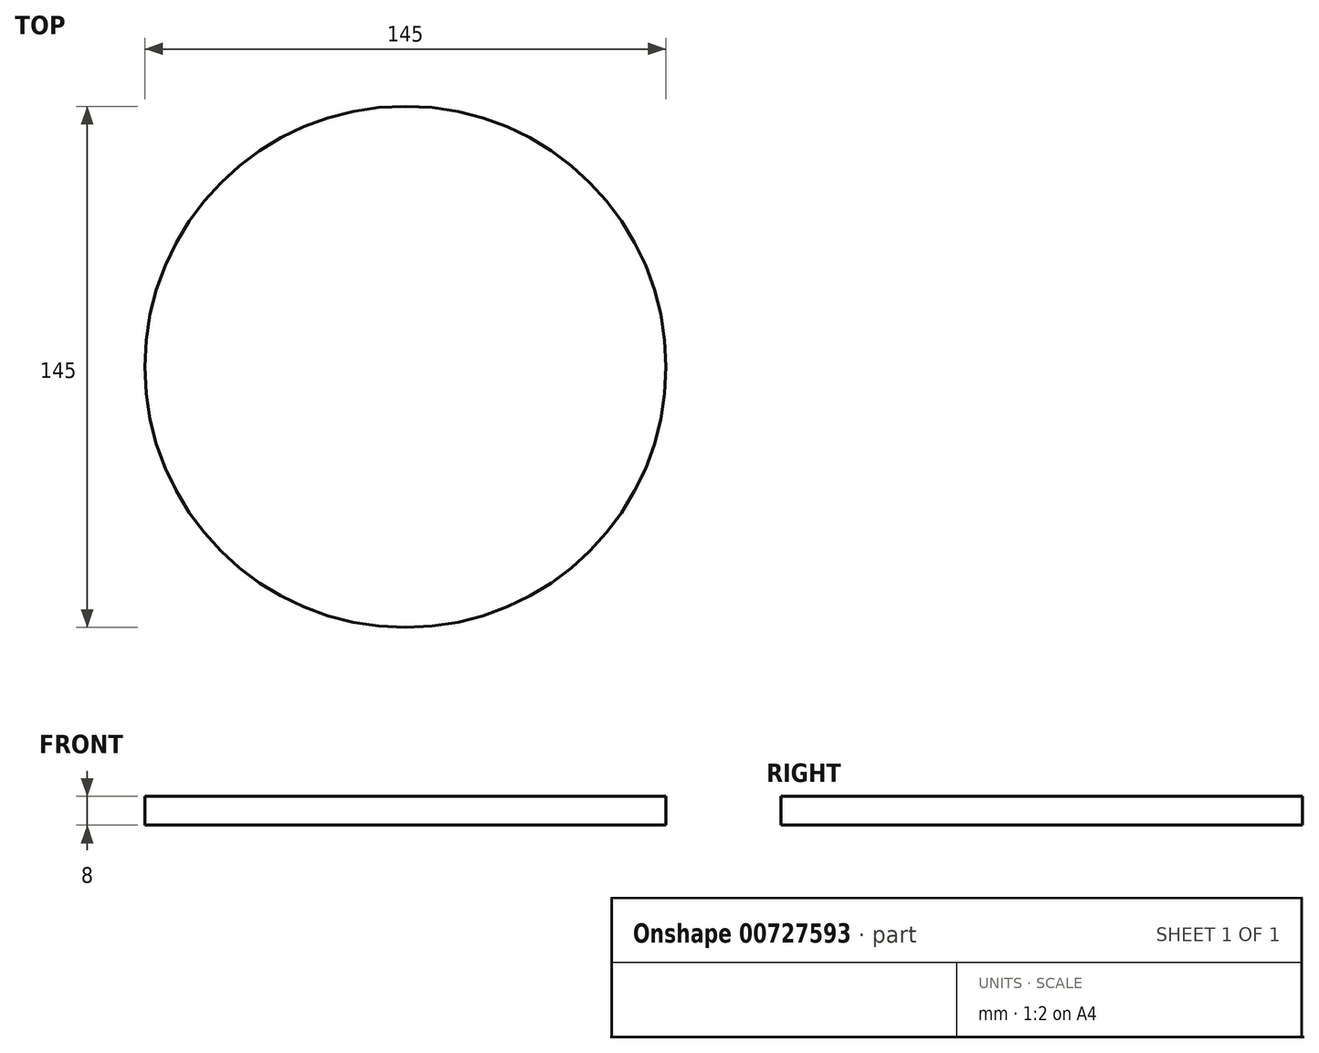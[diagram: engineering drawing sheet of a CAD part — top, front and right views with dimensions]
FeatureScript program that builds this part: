
annotation { "Feature Type Name" : "Feature", "Feature Type Description" : "" }
export const myFeature = defineFeature(function(context is Context, id is Id, definition is map)
    precondition{}
    {
        {
            var Q0;
            Q0=qCreatedBy(makeId("Top.planeOp"),FACE);
            var sketch = newSketch(context, id + "F0", { "sketchPlane" : qUnion([Q0])});
            skCircle(sketch, "E0", {"center": v(0, 0) * mm, "radius": 72.5 * mm});
            skSolve(sketch);
        }
        {
            var Q0;
            Q0=makeQuery(id+"F0.imprint","IMPRINT",FACE,{"disambiguationData":[TD([[makeQuery(id+"F0.imprint","IMPRINT",EDGE,{"derivedFrom":sQuery(id+"F0.wireOp",EDGE,"E0")}),1.0]])]});
            var Q1;
            Q1=sQuery(id+"F0.wireOp",EDGE,"E0");
            extrude(context, id + "F1", {"entities" : qUnion([Q0]), "surfaceEntities" : qUnion([Q1]), "depth" : 8 * mm, "offsetDistance" : 25.4 * mm});
        }
        {
            var Q0;
            Q0=qCreatedBy(makeId("Top.planeOp"),FACE);
            var sketch = newSketch(context, id + "F2", { "sketchPlane" : qUnion([Q0])});
            skLineSegment(sketch, "E1", {"start": v(-53.15, 29.78) * mm, "end": v(-22.76, 29.78) * mm});
            skLineSegment(sketch, "E2", {"start": v(-53.15, 29.78) * mm, "end": v(-53.15, 27.36) * mm});
            skLineSegment(sketch, "E3", {"start": v(-53.15, 27.36) * mm, "end": v(-39.89, 2.28) * mm});
            skLineSegment(sketch, "E4", {"start": v(-39.89, 2.28) * mm, "end": v(-33.01, 2.28) * mm});
            skLineSegment(sketch, "E5", {"start": v(-33.01, 2.28) * mm, "end": v(-45.31, 25.55) * mm});
            skLineSegment(sketch, "E6", {"start": v(-45.31, 25.55) * mm, "end": v(-33.01, 25.55) * mm});
            skLineSegment(sketch, "E7", {"start": v(-22.76, 29.78) * mm, "end": v(-21.8, 13.86) * mm});
            skLineSegment(sketch, "E8", {"start": v(-21.8, 13.86) * mm, "end": v(-22.76, 13.86) * mm});
            skFitSpline(sketch, "E9", {"points": [v(-33.01, 25.55) * mm, v(-29.28, 25.55) * mm], "startDerivative": vector(3.74, 0) * mm, "endDerivative": vector(3.74, 0) * mm});
            skFitSpline(sketch, "E10", {"points": [v(-29.28, 25.55) * mm, v(-27.1, 24.47) * mm, v(-24.7, 22.06) * mm, v(-23.6, 18.56) * mm, v(-22.76, 13.86) * mm], "startDerivative": vector(10.28, -4.32) * mm, "endDerivative": vector(2.93, -16.63) * mm});
            skLineSegment(sketch, "E11", {"start": v(-38.96, -4.23) * mm, "end": v(-53.5, -31.16) * mm});
            skLineSegment(sketch, "E12", {"start": v(-53.5, -31.16) * mm, "end": v(-53.5, -33.33) * mm});
            skLineSegment(sketch, "E13", {"start": v(-53.5, -33.33) * mm, "end": v(-22.5, -33.33) * mm});
            skLineSegment(sketch, "E14", {"start": v(-22.5, -33.33) * mm, "end": v(-20.46, -14.82) * mm});
            skLineSegment(sketch, "E15", {"start": v(-20.46, -14.82) * mm, "end": v(-21.8, -14.67) * mm});
            skLineSegment(sketch, "E16", {"start": v(-21.8, -14.67) * mm, "end": v(-23.65, -21.07) * mm});
            skLineSegment(sketch, "E17", {"start": v(-38.96, -4.23) * mm, "end": v(-35.52, -4.23) * mm});
            skLineSegment(sketch, "E18", {"start": v(-35.52, -4.23) * mm, "end": v(-47, -25.41) * mm});
            skLineSegment(sketch, "E19", {"start": v(-47, -25.41) * mm, "end": v(-30.28, -25.41) * mm});
            skFitSpline(sketch, "E20", {"points": [v(-30.28, -25.41) * mm, v(-27.22, -25.41) * mm, v(-25.69, -24.14) * mm, v(-23.65, -21.07) * mm], "startDerivative": vector(9.87, -1.12) * mm, "endDerivative": vector(5.6, 8.86) * mm});
            skLineSegment(sketch, "E21", {"start": v(-15.95, 29.78) * mm, "end": v(14.48, 29.78) * mm});
            skLineSegment(sketch, "E22", {"start": v(14.48, 29.78) * mm, "end": v(15.8, 13.98) * mm});
            skLineSegment(sketch, "E23", {"start": v(15.8, 13.98) * mm, "end": v(14.1, 13.83) * mm});
            skLineSegment(sketch, "E24", {"start": v(-15.95, 29.78) * mm, "end": v(-15.95, 27.2) * mm});
            skLineSegment(sketch, "E25", {"start": v(-15.95, 27.2) * mm, "end": v(-2.72, 2.45) * mm});
            skLineSegment(sketch, "E26", {"start": v(-2.72, 2.45) * mm, "end": v(3.7, 2.45) * mm});
            skLineSegment(sketch, "E27", {"start": v(3.7, 2.45) * mm, "end": v(-8.2, 25.89) * mm});
            skLineSegment(sketch, "E28", {"start": v(-8.2, 25.89) * mm, "end": v(3.7, 25.89) * mm});
            skFitSpline(sketch, "E29", {"points": [v(3.7, 25.89) * mm, v(6.54, 25.89) * mm, v(11.45, 22.86) * mm, v(13.34, 18.14) * mm, v(14.1, 13.83) * mm], "startDerivative": vector(12.95, 1.94) * mm, "endDerivative": vector(2.74, -17.01) * mm});
            skLineSegment(sketch, "E30", {"start": v(-1.59, -4.23) * mm, "end": v(-15.95, -31.2) * mm});
            skLineSegment(sketch, "E31", {"start": v(-15.95, -31.2) * mm, "end": v(-15.95, -33.09) * mm});
            skLineSegment(sketch, "E32", {"start": v(-15.95, -33.09) * mm, "end": v(14.86, -33.09) * mm});
            skLineSegment(sketch, "E33", {"start": v(14.86, -33.09) * mm, "end": v(16.94, -14.94) * mm});
            skLineSegment(sketch, "E34", {"start": v(16.94, -14.94) * mm, "end": v(15.2, -14.74) * mm});
            skLineSegment(sketch, "E35", {"start": v(-1.59, -4.23) * mm, "end": v(2.2, -4.23) * mm});
            skLineSegment(sketch, "E36", {"start": v(2.2, -4.23) * mm, "end": v(-9.15, -25.15) * mm});
            skLineSegment(sketch, "E37", {"start": v(-9.15, -25.15) * mm, "end": v(8.62, -25.15) * mm});
            skFitSpline(sketch, "E38", {"points": [v(8.62, -25.15) * mm, v(10.7, -25.15) * mm, v(13.72, -21.37) * mm, v(15.2, -14.74) * mm], "startDerivative": vector(8.85, -2.03) * mm, "endDerivative": vector(2.09, 16.45) * mm});
            skLineSegment(sketch, "E39", {"start": v(20.72, 28.9) * mm, "end": v(20.72, 26.83) * mm});
            skLineSegment(sketch, "E40", {"start": v(20.72, 28.9) * mm, "end": v(41.5, 28.9) * mm});
            skLineSegment(sketch, "E41", {"start": v(33.76, 26.45) * mm, "end": v(33.76, 2.45) * mm});
            skLineSegment(sketch, "E42", {"start": v(33.76, 2.45) * mm, "end": v(27.52, 2.45) * mm});
            skLineSegment(sketch, "E43", {"start": v(27.52, 2.45) * mm, "end": v(27.52, 23.05) * mm});
            skLineSegment(sketch, "E44", {"start": v(27.9, -4.23) * mm, "end": v(27.9, -26.66) * mm});
            skLineSegment(sketch, "E45", {"start": v(27.9, -4.23) * mm, "end": v(33.76, -4.23) * mm});
            skLineSegment(sketch, "E46", {"start": v(33.76, -4.23) * mm, "end": v(33.76, -26.66) * mm});
            skLineSegment(sketch, "E47", {"start": v(21.85, -31.2) * mm, "end": v(21.85, -33.28) * mm});
            skLineSegment(sketch, "E48", {"start": v(21.85, -33.28) * mm, "end": v(39.8, -33.28) * mm});
            skLineSegment(sketch, "E49", {"start": v(39.8, -33.28) * mm, "end": v(39.8, -31.2) * mm});
            skFitSpline(sketch, "E50", {"points": [v(21.85, -31.2) * mm, v(24.69, -31.2) * mm, v(27.14, -29.5) * mm, v(27.9, -26.66) * mm], "startDerivative": vector(8.65, -1.1) * mm, "endDerivative": vector(1.02, 9.06) * mm});
            skFitSpline(sketch, "E51", {"points": [v(33.76, -26.66) * mm, v(35.27, -29.68) * mm, v(37.54, -31.2) * mm, v(39.8, -31.2) * mm], "startDerivative": vector(3.38, -8.9) * mm, "endDerivative": vector(7.53, 0.94) * mm});
            skFitSpline(sketch, "E52", {"points": [v(20.72, 26.83) * mm, v(24.69, 26.83) * mm, v(26.58, 26.45) * mm, v(27.52, 23.05) * mm], "startDerivative": vector(12.27, 1.6) * mm, "endDerivative": vector(1.9, -11.53) * mm});
            skFitSpline(sketch, "E53", {"points": [v(33.76, 26.45) * mm, v(37.16, 26.45) * mm, v(39.8, 26.45) * mm, v(44.72, 23.05) * mm, v(47.56, 15.49) * mm, v(47.56, 9.82) * mm, v(45.48, 5.1) * mm, v(42.45, 2.64) * mm], "startDerivative": vector(27.45, -1.37) * mm, "endDerivative": vector(-25.11, -16.2) * mm});
            skFitSpline(sketch, "E54", {"points": [v(41.5, 28.9) * mm, v(41.7, 28.9) * mm, v(48.5, 26.45) * mm, v(54.93, 17.95) * mm, v(55.3, 9.63) * mm, v(53.23, 4.53) * mm, v(51.34, 2.45) * mm], "startDerivative": vector(22.9, 3.84) * mm, "endDerivative": vector(-16.3, -15.39) * mm});
            skLineSegment(sketch, "E55", {"start": v(42.45, 2.64) * mm, "end": v(51.34, 2.45) * mm});
            skSolve(sketch);
        }
        {
            var Q0;
            Q0=qCreatedBy(makeId("Top.planeOp"),FACE);
            var sketch = newSketch(context, id + "F3", { "sketchPlane" : qUnion([Q0])});
            skText(sketch, "E56", { "text": "The College of New Jersey", "fontName": "Arimo-Italic.ttf"});
            const initialGuessF3  = {"E56": [-0.0524, -0.00415, 1, 0, 0.00641]};
            skSetInitialGuess(sketch, initialGuessF3);
            skSolve(sketch);
        }
        {
            var Q0;
            Q0 = qSketchRegion(id + "F0", true);
            var Q1;
            Q1 = qConstructionFilter(qBodyType(qCreatedBy(id + "F2" ,EDGE), BodyType.WIRE), ConstructionObject.NO);
            extrude(context, id + "F4", {"entities" : qUnion([Q0]), "operationType" : NewBodyOperationType.REMOVE, "surfaceEntities" : qUnion([Q1]), "oppositeDirection" : true, "depth" : 0.5 * mm, "offsetDistance" : 25.4 * mm});
        }
        {
            var Q0;
            Q0 = qSketchRegion(id + "F3", true);
            extrude(context, id + "F5", {"entities" : qUnion([Q0]), "operationType" : NewBodyOperationType.REMOVE, "oppositeDirection" : true, "depth" : 6 * mm, "offsetDistance" : 25.4 * mm});
        }
    });
